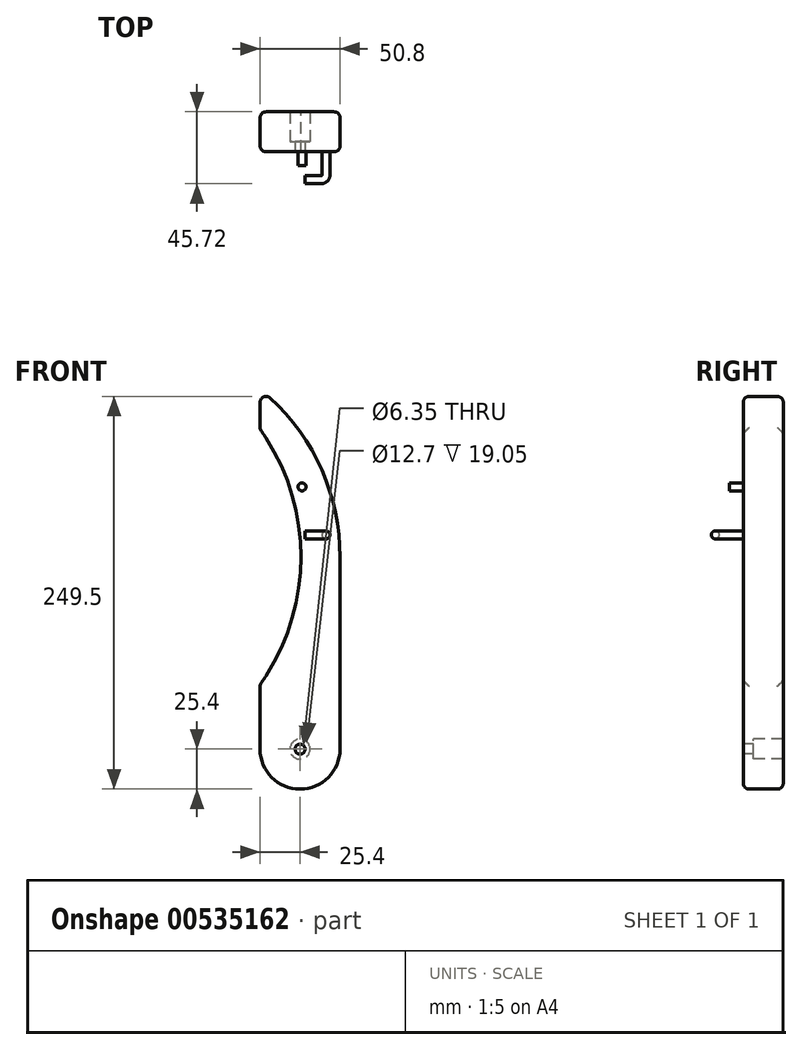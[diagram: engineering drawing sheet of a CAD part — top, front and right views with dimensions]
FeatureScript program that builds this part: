
annotation { "Feature Type Name" : "Feature", "Feature Type Description" : "" }
export const myFeature = defineFeature(function(context is Context, id is Id, definition is map)
    precondition{}
    {
        {
            var Q0;
            Q0=qCreatedBy(makeId("Front.planeOp"),FACE);
            var sketch = newSketch(context, id + "F0", { "sketchPlane" : qUnion([Q0])});
            skLineSegment(sketch, "E0.bottom", {"start": v(0, 0) * mm, "end": v(50.8, 0) * mm});
            skLineSegment(sketch, "E0.top", {"start": v(0, 254) * mm, "end": v(50.8, 254) * mm});
            skLineSegment(sketch, "E0.left", {"start": v(0, 0) * mm, "end": v(0, 254) * mm});
            skLineSegment(sketch, "E0.right", {"start": v(50.8, 0) * mm, "end": v(50.8, 254) * mm});
            skArc(sketch, "E1", {"start": v(0, 66.44) * mm, "mid": v(25.94, 147.52) * mm, "end": v(0, 228.6) * mm});
            skArc(sketch, "E2", {"start": v(0, 25.4) * mm, "mid": v(25.4, 0) * mm, "end": v(50.8, 25.4) * mm});
            skArc(sketch, "E3", {"start": v(0, 41.04) * mm, "mid": v(50.8, 147.52) * mm, "end": v(0, 254) * mm});
            skLineSegment(sketch, "E4", {"start": v(0, 25.4) * mm, "end": v(-155.84, 25.4) * mm});
            skSolve(sketch);
        }
        {
            var Q0;
            {var subQ4=sQuery(id+"F0.wireOp",EDGE,"E1");Q0=makeQuery(id+"F0.imprint","IMPRINT",FACE,{"disambiguationData":[TD([[makeQuery(id+"F0.imprint","IMPRINT",EDGE,{"derivedFrom":subQ4}),-1.0]])]});}
            var Q1;
            {var subQ0=sQuery(id+"F0.wireOp",EDGE,"E2");var subQ4=sQuery(id+"F0.wireOp",EDGE,"E0.left");var subQ5=makeQuery(id+"F0.imprint","INTERSECT",VERTEX,{"derivedFrom":[subQ4,subQ0]});Q1=makeQuery(id+"F0.imprint","IMPRINT",FACE,{"disambiguationData":[TD([[makeQuery(id+"F0.imprint","IMPRINT",EDGE,{"disambiguationData":[TD([[subQ5,-1.0]])],"derivedFrom":subQ4}),-1.0]])]});}
            extrude(context, id + "F1", {"entities" : qUnion([Q0, Q1]), "depth" : 25.4 * mm});
        }
        {
            var Q0;
            Q0=makeQuery(id+"F1.opExtrude","CAP_FACE",FACE,{"disambiguationData":[OSD([sQuery(id+"F0.wireOp",EDGE,"E0.bottom"),sQuery(id+"F0.wireOp",EDGE,"E0.top"),sQuery(id+"F0.wireOp",EDGE,"E0.left"),sQuery(id+"F0.wireOp",EDGE,"E0.right"),sQuery(id+"F0.wireOp",EDGE,"E1")])],"isStart":false});
            var sketch = newSketch(context, id + "F2", { "sketchPlane" : qUnion([Q0])});
            skCircle(sketch, "E5", {"center": v(25.4, 25.4) * mm, "radius": 3.18 * mm});
            skPoint(sketch, "E5.centerSnap0", {"position": v(25.4, 0) * mm});
            skSolve(sketch);
        }
        {
            var Q0;
            Q0=makeQuery(id+"F2.imprint","IMPRINT",FACE,{"disambiguationData":[TD([[makeQuery(id+"F2.imprint","IMPRINT",EDGE,{"derivedFrom":sQuery(id+"F2.wireOp",EDGE,"E5")}),1.0]])]});
            extrude(context, id + "F3", {"entities" : qUnion([Q0]), "operationType" : NewBodyOperationType.REMOVE, "oppositeDirection" : true, "depth" : 6.35 * mm});
        }
        {
            var Q0;
            {var subQ0=sQuery(id+"F0.wireOp",EDGE,"E0.left");Q0=makeQuery(id+"F1.opExtrude","SWEPT_FACE",FACE,{"disambiguationData":[OSD([subQ0]),TDD([makeQuery(id+"F0.imprint","IMPRINT",EDGE,{"disambiguationData":[TD([[makeQuery(id+"F0.imprint","INTERSECT",VERTEX,{"disambiguationData":[OD(1.0)],"derivedFrom":[subQ0,sQuery(id+"F0.wireOp",EDGE,"E1")]}),-1.0]])],"derivedFrom":subQ0})])]});}
            var Q1;
            {var subQ0=sQuery(id+"F0.wireOp",EDGE,"E0.left");Q1=makeQuery(id+"F1.opExtrude","SWEPT_FACE",FACE,{"disambiguationData":[OSD([subQ0]),TDD([makeQuery(id+"F0.imprint","IMPRINT",EDGE,{"disambiguationData":[TD([[makeQuery(id+"F0.imprint","INTERSECT",VERTEX,{"derivedFrom":[subQ0,sQuery(id+"F0.wireOp",EDGE,"E2")]}),-1.0]])],"derivedFrom":subQ0}),makeQuery(id+"F0.imprint","IMPRINT",EDGE,{"disambiguationData":[TD([[makeQuery(id+"F0.imprint","INTERSECT",VERTEX,{"disambiguationData":[OD(0.0)],"derivedFrom":[subQ0,sQuery(id+"F0.wireOp",EDGE,"E1")]}),1.0]])],"derivedFrom":subQ0})])]});}
            fillet(context, id + "F4", {"entities" : qUnion([Q0, Q1]), "radius" : 3.8 * mm, "tangentPropagation" : true, "allowEdgeOverflow" : false});
        }
        {
            var Q0;
            Q0=makeQuery(id+"F1.opExtrude","CAP_FACE",FACE,{"disambiguationData":[OSD([sQuery(id+"F0.wireOp",EDGE,"E0.left"),sQuery(id+"F0.wireOp",EDGE,"E0.right"),sQuery(id+"F0.wireOp",EDGE,"E1"),sQuery(id+"F0.wireOp",EDGE,"E2"),sQuery(id+"F0.wireOp",EDGE,"E3")])],"isStart":false});
            var sketch = newSketch(context, id + "F5", { "sketchPlane" : qUnion([Q0])});
            skCircle(sketch, "E6", {"center": v(26.63, 192) * mm, "radius": 2.54 * mm});
            skCircle(sketch, "E7", {"center": v(26.63, 192) * mm, "radius": 12.7 * mm, "construction": true});
            skCircle(sketch, "E8", {"center": v(26.63, 192) * mm, "radius": 6.35 * mm, "construction": true});
            skLineSegment(sketch, "E9", {"start": v(32.98, 192) * mm, "end": v(32.98, 161.5) * mm, "construction": true});
            skCircle(sketch, "E10", {"center": v(41.87, 161.5) * mm, "radius": 2.54 * mm});
            skSolve(sketch);
        }
        {
            var Q0;
            Q0=makeQuery(id+"F5.imprint","IMPRINT",FACE,{"disambiguationData":[TD([[makeQuery(id+"F5.imprint","IMPRINT",EDGE,{"derivedFrom":sQuery(id+"F5.wireOp",EDGE,"E6")}),1.0]])]});
            var Q1;
            Q1=makeQuery(id+"F5.imprint","IMPRINT",FACE,{"disambiguationData":[TD([[makeQuery(id+"F5.imprint","IMPRINT",EDGE,{"derivedFrom":sQuery(id+"F5.wireOp",EDGE,"E10")}),1.0]])]});
            extrude(context, id + "F6", {"entities" : qUnion([Q0, Q1]), "operationType" : NewBodyOperationType.ADD, "depth" : 8.9 * mm});
        }
        {
            var Q0;
            Q0=qCreatedBy(makeId("Top.planeOp"),FACE);
            cPlane(context, id + "F7", {"entities" : qUnion([Q0]), "cplaneType" : CPlaneType.OFFSET, "offset" : 161.5 * mm, "width" : 152.4 * mm, "height" : 152.4 * mm});
        }
        {
            var Q0;
            Q0=makeQuery(id+"F6.opExtrude","CAP_FACE",FACE,{"disambiguationData":[OSD([sQuery(id+"F5.wireOp",EDGE,"E10")])],"isStart":false});
            var sketch = newSketch(context, id + "F8", { "sketchPlane" : qUnion([Q0])});
            skCircle(sketch, "E11", {"center": v(41.87, 161.5) * mm, "radius": 2.54 * mm});
            skSolve(sketch);
        }
        {
            var Q0;
            Q0=qCreatedBy(id+"F7.planeOp",FACE);
            var sketch = newSketch(context, id + "F9", { "sketchPlane" : qUnion([Q0])});
            skLineSegment(sketch, "E12", {"start": v(41.87, -34.3) * mm, "end": v(41.87, -40.02) * mm});
            skLineSegment(sketch, "E13", {"start": v(38.7, -43.18) * mm, "end": v(28.54, -43.18) * mm});
            skPoint(sketch, "E14.visualSharp", {"position": v(41.87, -43.18) * mm});
            skArc(sketch, "E14.filletArc", {"start": v(38.7, -43.18) * mm, "mid": v(40.94, -42.25) * mm, "end": v(41.87, -40.02) * mm});
            skSolve(sketch);
        }
        {
            var Q0;
            Q0=makeQuery(id+"F8.imprint","IMPRINT",FACE,{"disambiguationData":[TD([[makeQuery(id+"F8.imprint","IMPRINT",EDGE,{"derivedFrom":sQuery(id+"F8.wireOp",EDGE,"E11")}),1.0]])]});
            var Q1;
            Q1=sQuery(id+"F9.wireOp",EDGE,"E12");
            var Q2;
            Q2=sQuery(id+"F9.wireOp",EDGE,"E14.filletArc");
            var Q3;
            Q3=sQuery(id+"F9.wireOp",EDGE,"E13");
            sweep(context, id + "F10", {"operationType" : NewBodyOperationType.ADD, "profiles" : qUnion([Q0]), "path" : qUnion([Q1, Q2, Q3])});
        }
        {
            var Q0;
            Q0=makeQuery(id+"F3.boolean.opBoolean","COPY",FACE,{"derivedFrom":makeQuery(id+"F3.opExtrude","CAP_FACE",FACE,{"disambiguationData":[OSD([sQuery(id+"F2.wireOp",EDGE,"E5")])],"isStart":false})});
            var sketch = newSketch(context, id + "F11", { "sketchPlane" : qUnion([Q0])});
            skCircle(sketch, "E15", {"center": v(25.4, 25.4) * mm, "radius": 6.35 * mm});
            skSolve(sketch);
        }
        {
            var Q0;
            Q0=qSketchRegion(id+"F11",true);
            extrude(context, id + "F12", {"entities" : qUnion([Q0]), "operationType" : NewBodyOperationType.REMOVE, "oppositeDirection" : true, "depth" : 25.4 * mm});
        }
        {
            var Q0;
            Q0=qCreatedBy(makeId("Front.planeOp"),FACE);
            var sketch = newSketch(context, id + "F13", { "sketchPlane" : qUnion([Q0])});
            skCircle(sketch, "E16", {"center": v(-122.15, 147.52) * mm, "radius": 139.7 * mm});
            skSolve(sketch);
        }
    });
